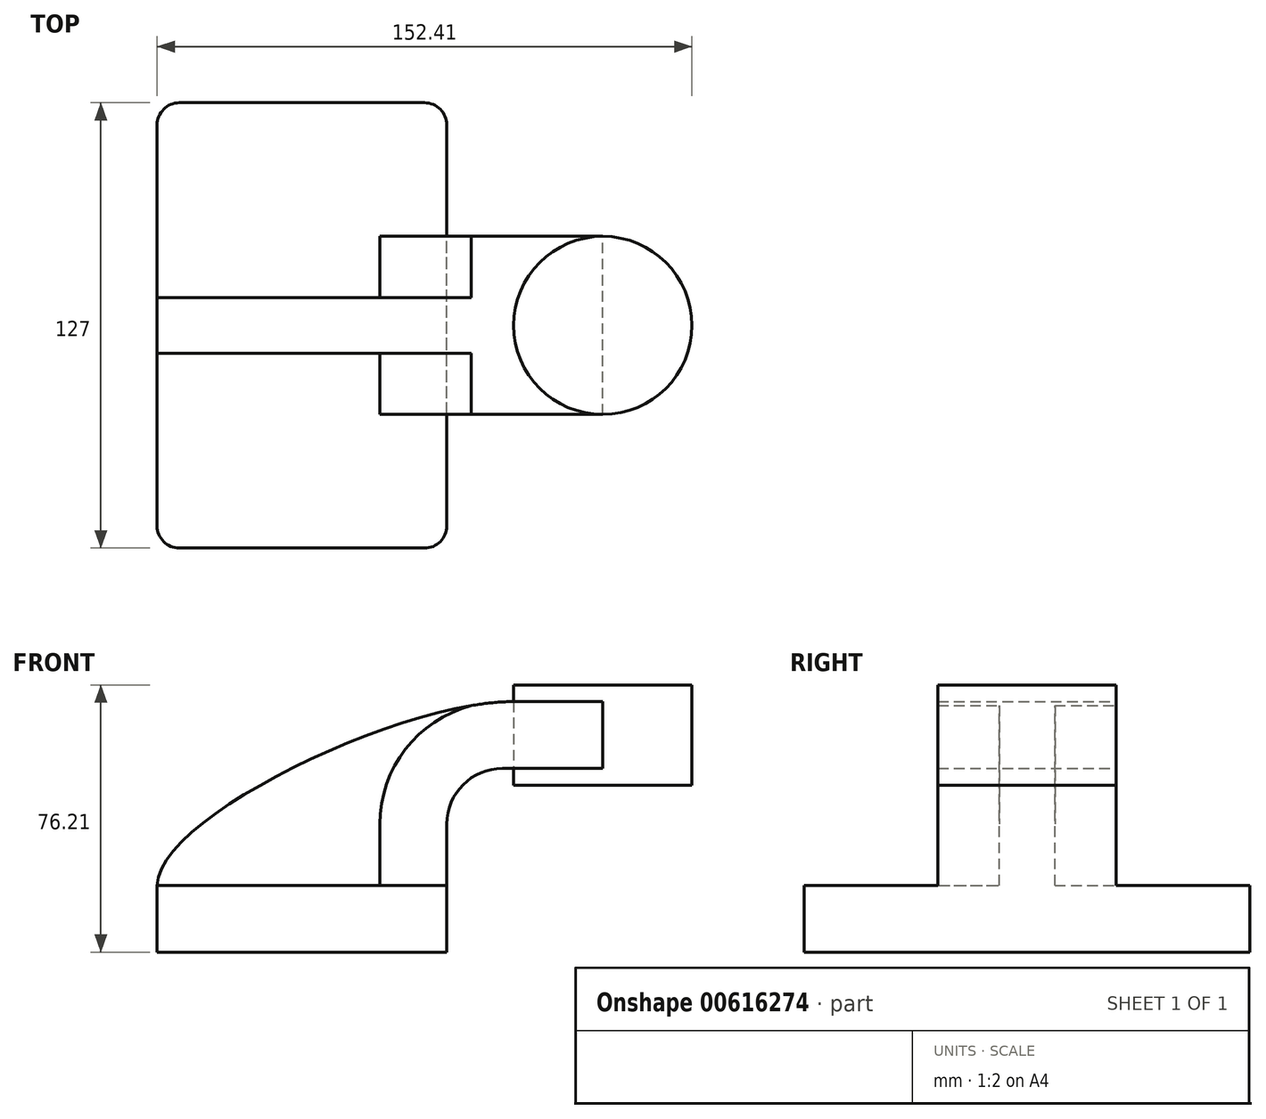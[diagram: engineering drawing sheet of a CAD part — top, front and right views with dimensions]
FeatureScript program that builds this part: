
annotation { "Feature Type Name" : "Feature", "Feature Type Description" : "" }
export const myFeature = defineFeature(function(context is Context, id is Id, definition is map)
    precondition{}
    {
        {
            var Q0;
            Q0=qCreatedBy(makeId("Front.planeOp"),FACE);
            var sketch = newSketch(context, id + "F0", { "sketchPlane" : qUnion([Q0])});
            skLineSegment(sketch, "E0.bottom", {"start": v(41.28, -9.52) * mm, "end": v(-41.28, -9.53) * mm});
            skLineSegment(sketch, "E0.top", {"start": v(41.27, 9.53) * mm, "end": v(-41.28, 9.53) * mm});
            skLineSegment(sketch, "E0.left", {"start": v(41.28, -9.52) * mm, "end": v(41.28, 9.53) * mm});
            skLineSegment(sketch, "E0.right", {"start": v(-41.28, -9.53) * mm, "end": v(-41.28, 9.53) * mm});
            skPoint(sketch, "E0.middle", {"position": v(0, 0) * mm});
            skLineSegment(sketch, "E1", {"start": v(41.27, 9.53) * mm, "end": v(41.27, 26.99) * mm});
            skLineSegment(sketch, "E2.bottom", {"start": v(111.12, 38.1) * mm, "end": v(60.33, 38.1) * mm});
            skLineSegment(sketch, "E2.top", {"start": v(111.12, 66.68) * mm, "end": v(60.33, 66.68) * mm});
            skLineSegment(sketch, "E2.left", {"start": v(111.12, 38.1) * mm, "end": v(111.12, 66.68) * mm});
            skLineSegment(sketch, "E2.right", {"start": v(60.33, 38.1) * mm, "end": v(60.33, 66.68) * mm});
            skPoint(sketch, "E2.middle", {"position": v(85.72, 52.39) * mm});
            skArc(sketch, "E3", {"start": v(41.27, 26.99) * mm, "mid": v(45.92, 38.21) * mm, "end": v(57.15, 42.86) * mm});
            skLineSegment(sketch, "E4", {"start": v(57.15, 42.86) * mm, "end": v(60.33, 42.86) * mm});
            skPoint(sketch, "E4.endSnap0", {"position": v(60.33, 52.39) * mm});
            skLineSegment(sketch, "E5.0", {"start": v(57.15, 61.91) * mm, "end": v(60.33, 61.91) * mm});
            skArc(sketch, "E5.1", {"start": v(22.23, 26.99) * mm, "mid": v(32.45, 51.68) * mm, "end": v(57.15, 61.91) * mm});
            skLineSegment(sketch, "E5.2", {"start": v(22.23, 9.53) * mm, "end": v(22.23, 26.99) * mm});
            skFitSpline(sketch, "E6", {"points": [v(-41.28, 9.53) * mm, v(60.33, 61.91) * mm], "startDerivative": vector(0, 57.5) * mm, "endDerivative": vector(98.72, 0) * mm});
            skLineSegment(sketch, "E7", {"start": v(85.72, 52.39) * mm, "end": v(85.72, 61.91) * mm});
            skLineSegment(sketch, "E8", {"start": v(85.72, 61.91) * mm, "end": v(60.33, 61.91) * mm});
            skLineSegment(sketch, "E9", {"start": v(85.72, 52.39) * mm, "end": v(85.72, 42.86) * mm});
            skLineSegment(sketch, "E10", {"start": v(85.72, 42.86) * mm, "end": v(60.33, 42.86) * mm});
            skLineSegment(sketch, "E11", {"start": v(85.72, 61.91) * mm, "end": v(85.72, 66.68) * mm});
            skLineSegment(sketch, "E12", {"start": v(85.72, 42.86) * mm, "end": v(85.72, 38.1) * mm});
            skLineSegment(sketch, "E13", {"start": v(85.72, 38.1) * mm, "end": v(85.72, 42.86) * mm});
            skSolve(sketch);
        }
        {
            var Q0;
            Q0=makeQuery(id+"F0.imprint","IMPRINT",FACE,{"disambiguationData":[TD([[makeQuery(id+"F0.imprint","IMPRINT",EDGE,{"derivedFrom":sQuery(id+"F0.wireOp",EDGE,"E0.bottom")}),-1.0]])]});
            extrude(context, id + "F1", {"entities" : qUnion([Q0]), "endBound" : BoundingType.SYMMETRIC, "depth" : 127 * mm, "offsetDistance" : 25.4 * mm});
        }
        {
            var Q0;
            {var subQ3=sQuery(id+"F0.wireOp",EDGE,"E1");Q0=makeQuery(id+"F0.imprint","IMPRINT",FACE,{"disambiguationData":[TD([[makeQuery(id+"F0.imprint","IMPRINT",EDGE,{"derivedFrom":subQ3}),1.0]])]});}
            var Q1;
            Q1=makeQuery(id+"F0.imprint","IMPRINT",FACE,{"disambiguationData":[TD([[makeQuery(id+"F0.imprint","IMPRINT",EDGE,{"derivedFrom":sQuery(id+"F0.wireOp",EDGE,"E7")}),1.0]])]});
            extrude(context, id + "F2", {"entities" : qUnion([Q0, Q1]), "operationType" : NewBodyOperationType.ADD, "endBound" : BoundingType.SYMMETRIC, "depth" : 50.8 * mm, "offsetDistance" : 25.4 * mm});
        }
        {
            var Q0;
            {var subQ3=sQuery(id+"F0.wireOp",EDGE,"E5.2");Q0=makeQuery(id+"F0.imprint","IMPRINT",FACE,{"disambiguationData":[TD([[makeQuery(id+"F0.imprint","IMPRINT",EDGE,{"derivedFrom":subQ3}),1.0]])]});}
            extrude(context, id + "F3", {"entities" : qUnion([Q0]), "operationType" : NewBodyOperationType.ADD, "endBound" : BoundingType.SYMMETRIC, "depth" : 15.88 * mm, "offsetDistance" : 25.4 * mm});
        }
        {
            var Q0;
            {var subQ0=sQuery(id+"F0.wireOp",EDGE,"E2.left");Q0=makeQuery(id+"F0.imprint","IMPRINT",FACE,{"disambiguationData":[TD([[makeQuery(id+"F0.imprint","IMPRINT",EDGE,{"derivedFrom":subQ0}),1.0]])]});}
            var Q1;
            Q1=sQuery(id+"F0.wireOp",EDGE,"E7");
            revolve(context, id + "F4", {"entities" : qUnion([Q0]), "axis" : qUnion([Q1]), "revolveType" : RevolveType.FULL});
        }
        {
            var Q0;
            Q0=makeQuery(id+"F1.opExtrude","CAP_EDGE",EDGE,{"disambiguationData":[OSD([sQuery(id+"F0.wireOp",EDGE,"E0.left")])],"isStart":false});
            var Q1;
            Q1=makeQuery(id+"F1.opExtrude","CAP_EDGE",EDGE,{"disambiguationData":[OSD([sQuery(id+"F0.wireOp",EDGE,"E0.right")])],"isStart":false});
            var Q2;
            Q2=makeQuery(id+"F1.opExtrude","CAP_EDGE",EDGE,{"disambiguationData":[OSD([sQuery(id+"F0.wireOp",EDGE,"E0.right")])],"isStart":true});
            var Q3;
            Q3=makeQuery(id+"F1.opExtrude","CAP_EDGE",EDGE,{"disambiguationData":[OSD([sQuery(id+"F0.wireOp",EDGE,"E0.left")])],"isStart":true});
            fillet(context, id + "F5", {"entities" : qUnion([Q0, Q1, Q2, Q3]), "radius" : 6.35 * mm, "tangentPropagation" : true, "allowEdgeOverflow" : false});
        }
        {
            var Q0;
            Q0=makeQuery(id+"F4.opRevolve","SWEPT_BODY",BODY,{"disambiguationData":[OSD([sQuery(id+"F0.wireOp",EDGE,"E2.bottom"),sQuery(id+"F0.wireOp",EDGE,"E2.top"),sQuery(id+"F0.wireOp",EDGE,"E2.left"),sQuery(id+"F0.wireOp",EDGE,"E7"),sQuery(id+"F0.wireOp",EDGE,"E9"),sQuery(id+"F0.wireOp",EDGE,"E11"),sQuery(id+"F0.wireOp",EDGE,"E13")])]});
            deleteBodies(context, id + "F6", {"entities" : qUnion([Q0])});
        }
        {
            var Q0;
            {var subQ0=sQuery(id+"F0.wireOp",EDGE,"E2.left");Q0=makeQuery(id+"F0.imprint","IMPRINT",FACE,{"disambiguationData":[TD([[makeQuery(id+"F0.imprint","IMPRINT",EDGE,{"derivedFrom":subQ0}),1.0]])]});}
            var Q1;
            Q1=sQuery(id+"F0.wireOp",EDGE,"E7");
            revolve(context, id + "F7", {"entities" : qUnion([Q0]), "axis" : qUnion([Q1]), "revolveType" : RevolveType.FULL});
        }
    });
